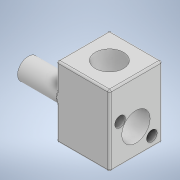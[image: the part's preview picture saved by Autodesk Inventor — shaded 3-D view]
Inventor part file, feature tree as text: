
AUTODESK INVENTOR PART (.ipt)
format: ipt  version: 2022 (Build 260153000, 153)  size: 184,832 bytes
history: native  units: mm
features: sketch x5, extrude x3, hole x2, other x1, fillet x1
ambient origin geometry x8: Origin, YZ Plane, XZ Plane, XY Plane, X Axis, Y Axis, Z Axis, Center Point
bodies: Body1 (feature_tree)
feature tree (12):
  other  "Sólido1"
  extrude  "Extrusão1"  Depth=15.0mm
  hole  "Furo1"  [1 undecoded]
  hole  "Furo2"  [1 undecoded]
  extrude  "Extrusão2"  Depth=0.5mm
  extrude  "Extrusão3"  Depth=0.5mm
  fillet  "Arredondamento2"  Radius=11.0mm
  sketch  "Esboço1"  dims[d0=15.0mm d1=15.0mm]
  sketch  "Esboço2"  dims[d2=20.0mm d3=0.0mm]
  sketch  "Esboço4"  dims[d4=8.0mm d5=6.0mm d6=4.0mm d7=2.0mm d8=90.0deg d9=12.0mm d10=0.0mm]
  sketch  "Esboço5"  dims[d11=8.0mm d12=6.0mm d13=4.0mm d14=2.0mm d15=90.0deg d16=7.5mm d17=0.0mm d19=3.0mm]
  sketch  "Esboço6"  dims[d20=3.0mm d21=0.0mm d22=0.0mm d23=6.0mm d24=6.0mm d25=11.0mm d26=0.0mm d27=0.5mm]
note: 2 required parameter values undecoded (feature->parameter linkage not recoverable at this tier; creation-order binding heuristic only, values carry confidence <= 0.55)
